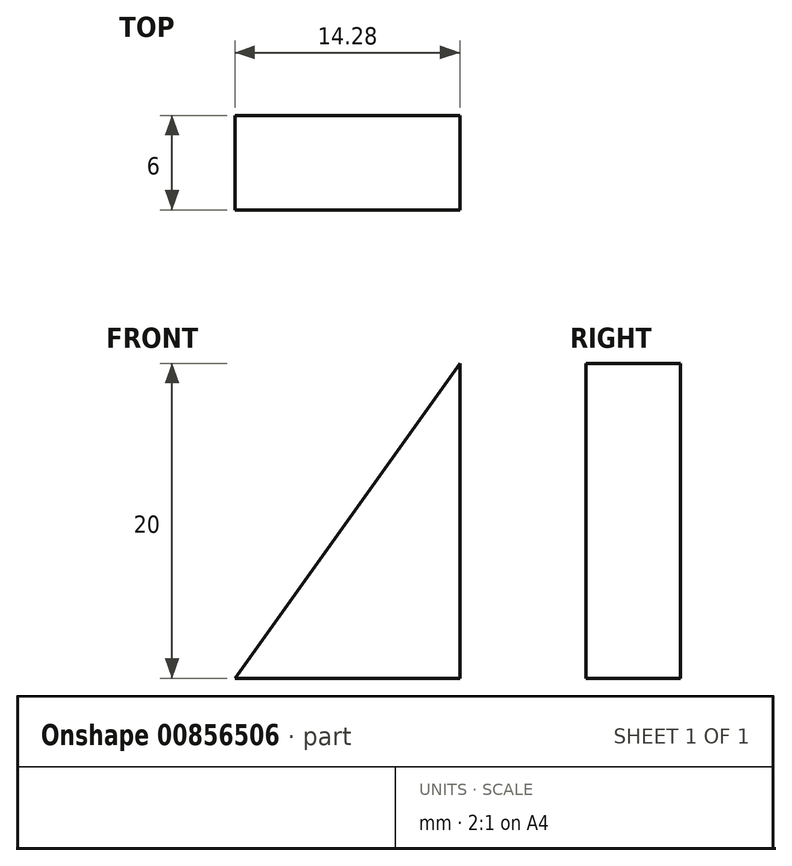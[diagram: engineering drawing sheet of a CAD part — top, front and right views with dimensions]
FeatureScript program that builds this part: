
annotation { "Feature Type Name" : "Feature", "Feature Type Description" : "" }
export const myFeature = defineFeature(function(context is Context, id is Id, definition is map)
    precondition{}
    {
        {
            var Q0;
            Q0=qCreatedBy(makeId("Top.planeOp"),FACE);
            var sketch = newSketch(context, id + "F0", { "sketchPlane" : qUnion([Q0])});
            skLineSegment(sketch, "E0.bottom", {"start": v(7.14, 3) * mm, "end": v(-7.14, 3) * mm});
            skLineSegment(sketch, "E0.top", {"start": v(7.14, -3) * mm, "end": v(-7.14, -3) * mm});
            skLineSegment(sketch, "E0.left", {"start": v(7.14, 3) * mm, "end": v(7.14, -3) * mm});
            skLineSegment(sketch, "E0.right", {"start": v(-7.14, 3) * mm, "end": v(-7.14, -3) * mm});
            skPoint(sketch, "E0.middle", {"position": v(0, 0) * mm});
            skSolve(sketch);
        }
        {
            var Q0;
            Q0 = qSketchRegion(id + "F0", true);
            var Q1;
            Q1=makeQuery(id+"F0.imprint","IMPRINT",FACE,{"disambiguationData":[TD([[makeQuery(id+"F0.imprint","IMPRINT",EDGE,{"derivedFrom":sQuery(id+"F0.wireOp",EDGE,"E0.bottom")}),1.0]])]});
            extrude(context, id + "F1", {"entities" : qUnion([Q0, Q1]), "depth" : 20 * mm, "offsetDistance" : 25 * mm});
        }
        {
            var Q0;
            Q0=makeQuery(id+"F1.opExtrude","CAP_EDGE",EDGE,{"disambiguationData":[OSD([sQuery(id+"F0.wireOp",EDGE,"E0.right")])],"isStart":false});
            chamfer(context, id + "F2", {"entities" : qUnion([Q0]), "chamferType" : ChamferType.TWO_OFFSETS, "width1" : 14.28 * mm, "oppositeDirection" : false, "width2" : 20 * mm, "tangentPropagation" : true});
        }
    });
